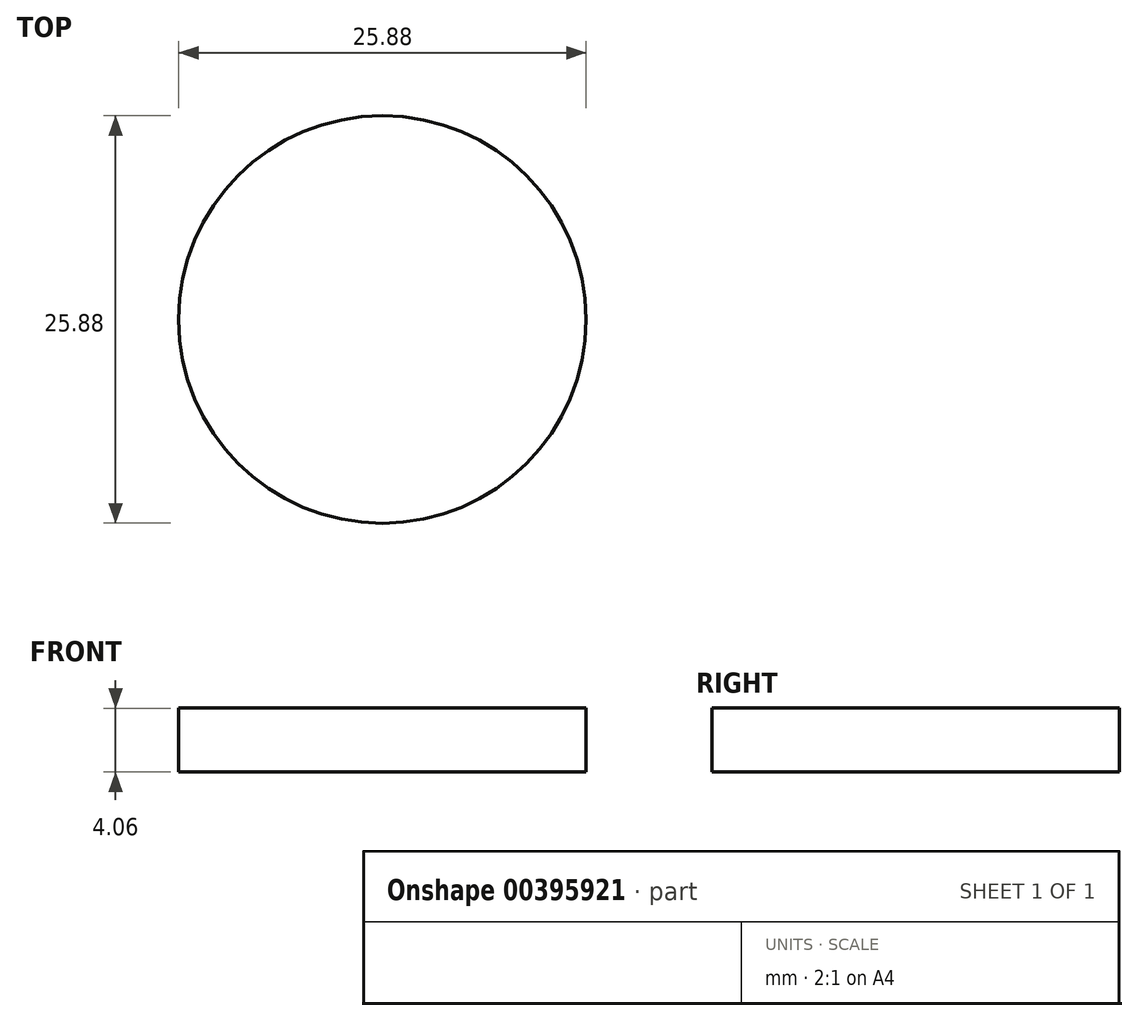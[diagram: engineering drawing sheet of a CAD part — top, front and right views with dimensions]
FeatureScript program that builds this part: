
annotation { "Feature Type Name" : "Feature", "Feature Type Description" : "" }
export const myFeature = defineFeature(function(context is Context, id is Id, definition is map)
    precondition{}
    {
        {
            var Q0;
            Q0=qCreatedBy(makeId("Top.planeOp"),FACE);
            var sketch = newSketch(context, id + "F0", { "sketchPlane" : qUnion([Q0])});
            skCircle(sketch, "E0", {"center": v(0, 0) * mm, "radius": 12.94 * mm});
            skSolve(sketch);
        }
        {
            var Q0;
            Q0=makeQuery(id+"F0.imprint","IMPRINT",FACE,{"disambiguationData":[TD([[makeQuery(id+"F0.imprint","IMPRINT",EDGE,{"derivedFrom":sQuery(id+"F0.wireOp",EDGE,"E0")}),1.0]])]});
            extrude(context, id + "F1", {"entities" : qUnion([Q0]), "depth" : 4.06 * mm});
        }
    });
